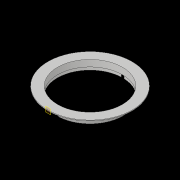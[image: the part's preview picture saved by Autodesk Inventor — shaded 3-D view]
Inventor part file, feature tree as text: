
AUTODESK INVENTOR PART (.ipt)
format: ipt  version: 2017 (Build 210142000, 142)  size: 137,216 bytes
history: native  units: in
note: dims shown in document units (in); Inventor stores cm internally (conversion verified against a paired STEP export)
features: sketch x2, revolve x1, plane x1, extrude x1
ambient origin geometry x8: Origin, YZ Plane, XZ Plane, XY Plane, X Axis, Y Axis, Z Axis, Center Point
bodies: Solid1 (feature_tree)
feature tree (5):
  revolve  "Revolution1"  [1 undecoded]
  plane  "Work Plane1"
  extrude  "Extrusion1"  Depth=0.25in
  sketch  "Sketch1"  dims[d0=2.0in d1=5.4375in]
  sketch  "Sketch2"  dims[d2=1.25in d3=0.125in d4=0.125in d5=2.25in d6=1.5in d7=0.125in d8=90.0deg d9=0.5in d10=1.0285in d11=1.0in d12=0.0in d13=1.0285in d14=0.0625in d15=0.25in d16=0.25in]
note: 1 required parameter value undecoded (feature->parameter linkage not recoverable at this tier; creation-order binding heuristic only, values carry confidence <= 0.55)
